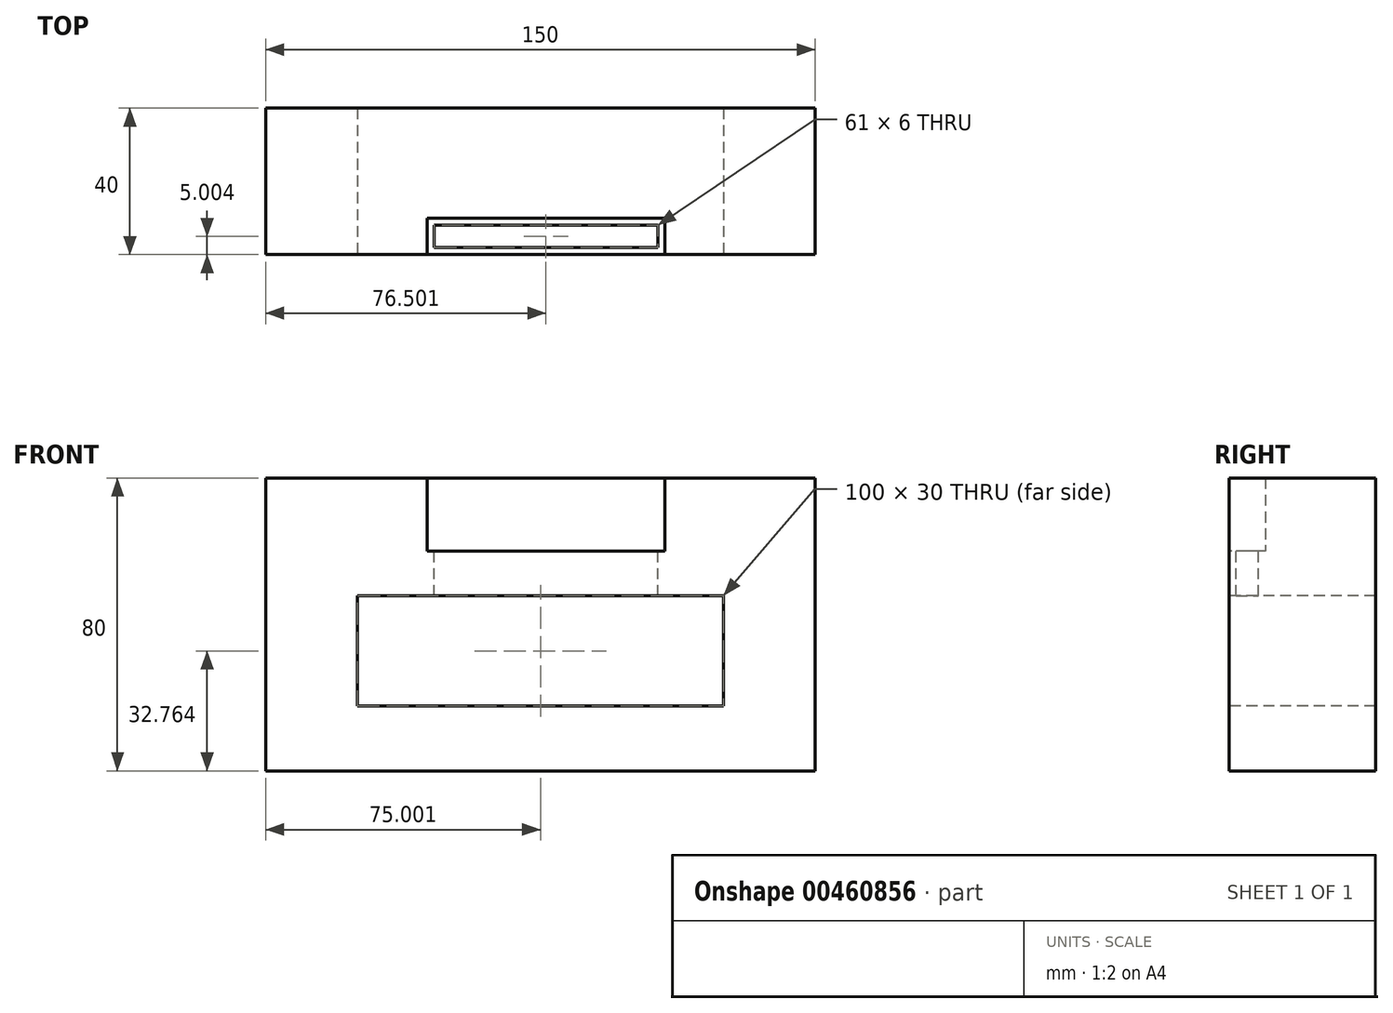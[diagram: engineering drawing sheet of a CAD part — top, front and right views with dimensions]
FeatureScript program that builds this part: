
annotation { "Feature Type Name" : "Feature", "Feature Type Description" : "" }
export const myFeature = defineFeature(function(context is Context, id is Id, definition is map)
    precondition{}
    {
        {
            var Q0;
            Q0=qCreatedBy(makeId("Top.planeOp"),FACE);
            var sketch = newSketch(context, id + "F0", { "sketchPlane" : qUnion([Q0])});
            skLineSegment(sketch, "E0.bottom", {"start": v(-75.19, -12.19) * mm, "end": v(74.81, -12.19) * mm});
            skLineSegment(sketch, "E0.top", {"start": v(-75.19, 27.81) * mm, "end": v(74.81, 27.81) * mm});
            skLineSegment(sketch, "E0.left", {"start": v(-75.19, -12.19) * mm, "end": v(-75.19, 27.81) * mm});
            skLineSegment(sketch, "E0.right", {"start": v(74.81, -12.19) * mm, "end": v(74.81, 27.81) * mm});
            skSolve(sketch);
        }
        {
            var Q0;
            Q0 = qSketchRegion(id + "F0", true);
            extrude(context, id + "F1", {"entities" : qUnion([Q0]), "depth" : 80 * mm});
        }
        {
            var Q0;
            Q0=makeQuery(id+"F1.opExtrude","SWEPT_FACE",FACE,{"disambiguationData":[OSD([sQuery(id+"F0.wireOp",EDGE,"E0.bottom")])]});
            var sketch = newSketch(context, id + "F2", { "sketchPlane" : qUnion([Q0])});
            skLineSegment(sketch, "E1.bottom", {"start": v(-31.19, 80) * mm, "end": v(33.81, 80) * mm});
            skLineSegment(sketch, "E1.top", {"start": v(-31.19, 60) * mm, "end": v(33.81, 60) * mm});
            skLineSegment(sketch, "E1.left", {"start": v(-31.19, 80) * mm, "end": v(-31.19, 60) * mm});
            skLineSegment(sketch, "E1.right", {"start": v(33.81, 80) * mm, "end": v(33.81, 60) * mm});
            skSolve(sketch);
        }
        {
            var Q0;
            Q0 = qSketchRegion(id + "F2", true);
            extrude(context, id + "F3", {"entities" : qUnion([Q0]), "operationType" : NewBodyOperationType.REMOVE, "oppositeDirection" : true, "depth" : 10 * mm});
        }
        {
            var Q0;
            Q0=makeQuery(id+"F1.opExtrude","SWEPT_FACE",FACE,{"disambiguationData":[OSD([sQuery(id+"F0.wireOp",EDGE,"E0.bottom")])]});
            var sketch = newSketch(context, id + "F4", { "sketchPlane" : qUnion([Q0])});
            skLineSegment(sketch, "E2.bottom", {"start": v(-50.19, 47.76) * mm, "end": v(49.81, 47.76) * mm});
            skLineSegment(sketch, "E2.top", {"start": v(-50.19, 17.76) * mm, "end": v(49.81, 17.76) * mm});
            skLineSegment(sketch, "E2.left", {"start": v(-50.19, 47.76) * mm, "end": v(-50.19, 17.76) * mm});
            skLineSegment(sketch, "E2.right", {"start": v(49.81, 47.76) * mm, "end": v(49.81, 17.76) * mm});
            skSolve(sketch);
        }
        {
            var Q0;
            Q0 = qSketchRegion(id + "F4", true);
            extrude(context, id + "F5", {"entities" : qUnion([Q0]), "operationType" : NewBodyOperationType.REMOVE, "oppositeDirection" : true, "depth" : 87.2 * mm});
        }
        {
            var Q0;
            Q0=makeQuery(id+"F3.boolean.opBoolean","COPY",FACE,{"derivedFrom":makeQuery(id+"F3.opExtrude","SWEPT_FACE",FACE,{"disambiguationData":[OSD([sQuery(id+"F2.wireOp",EDGE,"E1.top")])]})});
            var sketch = newSketch(context, id + "F6", { "sketchPlane" : qUnion([Q0])});
            skLineSegment(sketch, "E3.bottom", {"start": v(-29.19, -4.19) * mm, "end": v(31.81, -4.19) * mm});
            skLineSegment(sketch, "E3.top", {"start": v(-29.19, -10.19) * mm, "end": v(31.81, -10.19) * mm});
            skLineSegment(sketch, "E3.left", {"start": v(-29.19, -4.19) * mm, "end": v(-29.19, -10.19) * mm});
            skLineSegment(sketch, "E3.right", {"start": v(31.81, -4.19) * mm, "end": v(31.81, -10.19) * mm});
            skPoint(sketch, "E4.orphan", {"position": v(-29.19, -12.19) * mm});
            skSolve(sketch);
        }
        {
            var Q0;
            Q0=makeQuery(id+"F6.imprint","IMPRINT",FACE,{"disambiguationData":[TD([[makeQuery(id+"F6.imprint","IMPRINT",EDGE,{"derivedFrom":sQuery(id+"F6.wireOp",EDGE,"E3.bottom")}),-1.0]])]});
            extrude(context, id + "F7", {"entities" : qUnion([Q0]), "operationType" : NewBodyOperationType.REMOVE, "oppositeDirection" : true, "depth" : 25 * mm});
        }
    });
